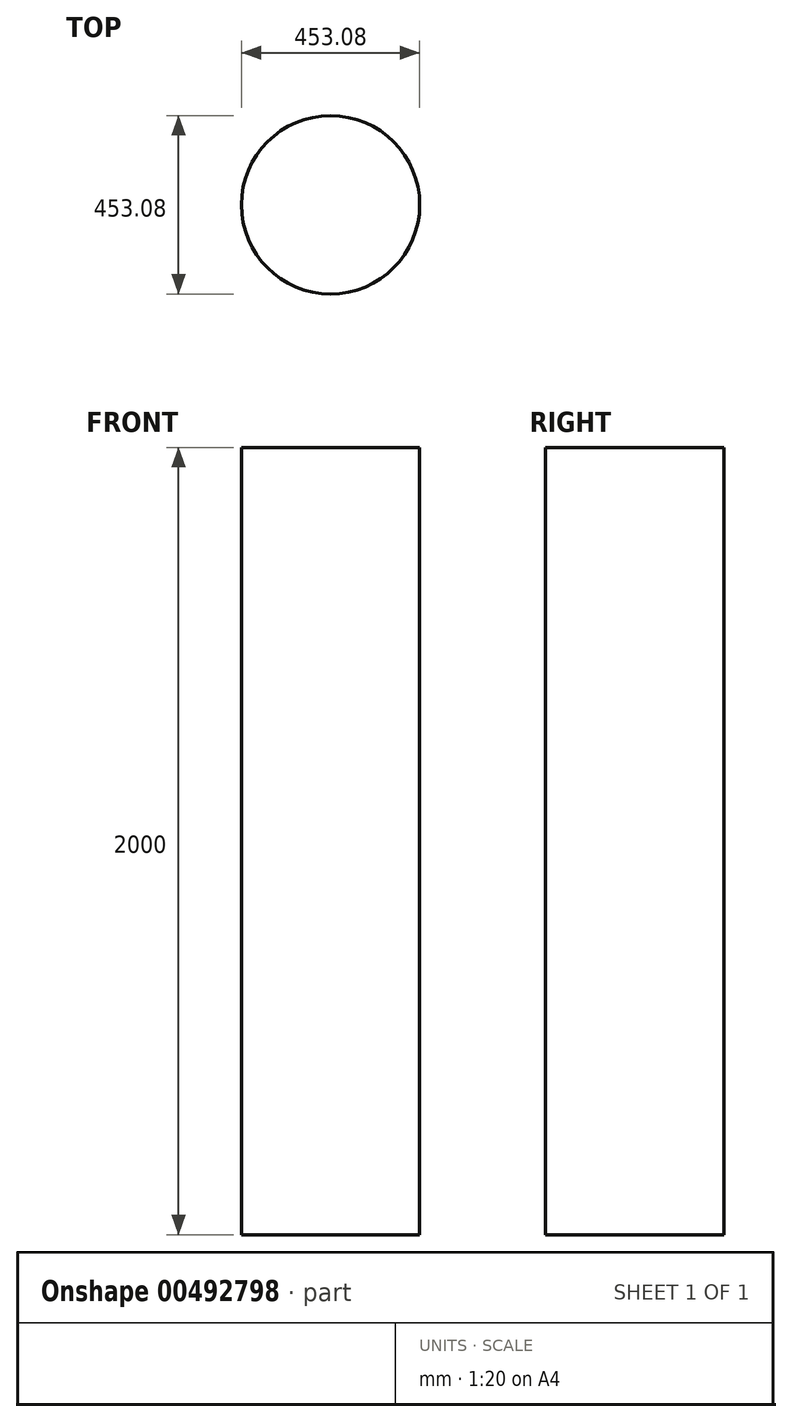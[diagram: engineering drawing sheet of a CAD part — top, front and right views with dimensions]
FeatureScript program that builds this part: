
annotation { "Feature Type Name" : "Feature", "Feature Type Description" : "" }
export const myFeature = defineFeature(function(context is Context, id is Id, definition is map)
    precondition{}
    {
        {
            var Q0;
            Q0=qCreatedBy(makeId("Top.planeOp"),FACE);
            var sketch = newSketch(context, id + "F0", { "sketchPlane" : qUnion([Q0])});
            skCircle(sketch, "E0", {"center": v(0, 0) * mm, "radius": 226.54 * mm});
            skSolve(sketch);
        }
        {
            var Q0;
            Q0=makeQuery(id+"F0.imprint","IMPRINT",FACE,{"disambiguationData":[TD([[makeQuery(id+"F0.imprint","IMPRINT",EDGE,{"derivedFrom":sQuery(id+"F0.wireOp",EDGE,"E0")}),1.0]])]});
            extrude(context, id + "F1", {"entities" : qUnion([Q0]), "depth" : 2000 * mm});
        }
    });
